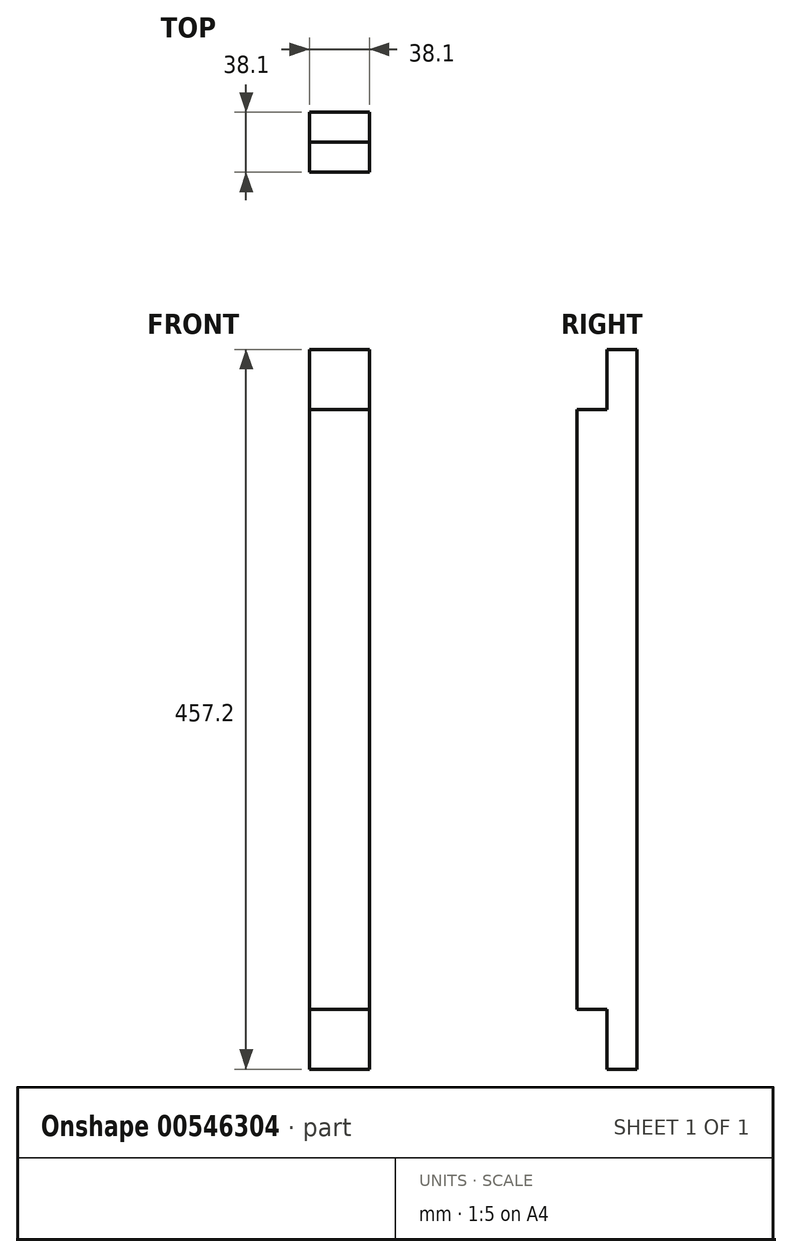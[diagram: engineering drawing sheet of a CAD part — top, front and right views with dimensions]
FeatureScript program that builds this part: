
annotation { "Feature Type Name" : "Feature", "Feature Type Description" : "" }
export const myFeature = defineFeature(function(context is Context, id is Id, definition is map)
    precondition{}
    {
        {
            var Q0;
            Q0=qCreatedBy(makeId("Top.planeOp"),FACE);
            var sketch = newSketch(context, id + "F0", { "sketchPlane" : qUnion([Q0])});
            skLineSegment(sketch, "E0", {"start": v(-74.13, 47.73) * mm, "end": v(-36.03, 47.73) * mm});
            skLineSegment(sketch, "E1", {"start": v(-36.03, 47.73) * mm, "end": v(-36.03, 9.63) * mm});
            skLineSegment(sketch, "E2", {"start": v(-36.03, 9.63) * mm, "end": v(-74.13, 9.63) * mm});
            skLineSegment(sketch, "E3", {"start": v(-74.13, 9.63) * mm, "end": v(-74.13, 47.73) * mm});
            skSolve(sketch);
        }
        {
            var Q0;
            Q0 = qSketchRegion(id + "F0", true);
            extrude(context, id + "F1", {"entities" : qUnion([Q0]), "depth" : 457.2 * mm, "offsetDistance" : 25.4 * mm});
        }
        {
            var Q0;
            Q0=makeQuery(id+"F1.opExtrude","SWEPT_FACE",FACE,{"disambiguationData":[OSD([sQuery(id+"F0.wireOp",EDGE,"E2")])]});
            var sketch = newSketch(context, id + "F2", { "sketchPlane" : qUnion([Q0])});
            skLineSegment(sketch, "E4", {"start": v(-36.03, 0) * mm, "end": v(-36.03, 38.1) * mm});
            skLineSegment(sketch, "E5", {"start": v(-36.03, 38.1) * mm, "end": v(-74.13, 38.1) * mm});
            skLineSegment(sketch, "E6", {"start": v(-74.13, 38.1) * mm, "end": v(-74.13, 0) * mm});
            skLineSegment(sketch, "E7", {"start": v(-74.13, 0) * mm, "end": v(-36.03, 0) * mm});
            skLineSegment(sketch, "E8", {"start": v(-36.03, 457.2) * mm, "end": v(-36.03, 419.1) * mm});
            skLineSegment(sketch, "E9", {"start": v(-36.03, 419.1) * mm, "end": v(-74.13, 419.1) * mm});
            skLineSegment(sketch, "E10", {"start": v(-74.13, 419.1) * mm, "end": v(-74.13, 457.2) * mm});
            skLineSegment(sketch, "E11", {"start": v(-74.13, 457.2) * mm, "end": v(-36.03, 457.2) * mm});
            skSolve(sketch);
        }
        {
            var Q0;
            Q0 = qSketchRegion(id + "F2", true);
            extrude(context, id + "F3", {"entities" : qUnion([Q0]), "operationType" : NewBodyOperationType.REMOVE, "oppositeDirection" : true, "depth" : 19.05 * mm, "offsetDistance" : 25.4 * mm});
        }
    });
